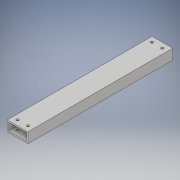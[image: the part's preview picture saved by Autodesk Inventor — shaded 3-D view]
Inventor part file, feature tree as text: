
AUTODESK INVENTOR PART (.ipt)
format: ipt  version: 2017 (Build 210142000, 142)  size: 117,248 bytes
history: native  units: in
note: dims shown in document units (in); Inventor stores cm internally (conversion verified against a paired STEP export)
features: sketch x2, extrude x1, hole x1
ambient origin geometry x8: Origin, YZ Plane, XZ Plane, XY Plane, X Axis, Y Axis, Z Axis, Center Point
bodies: Solid1 (feature_tree)
feature tree (4):
  extrude  "Extrusion1"  Depth=1.0in
  hole  "Hole1"  [1 undecoded]
  sketch  "Sketch1"  dims[d0=2.0in d1=1.0in]
  sketch  "Sketch2"  dims[d2=1.75in d3=0.75in d4=0.125in d5=0.125in d6=14.0in d7=0.0in d8=0.25in d9=0.5in d10=0.5in d11=0.25in d12=0.75in d13=0.375in d14=0.25in d15=0.5635in d16=1.0in d17=0.8108in]
note: 1 required parameter value undecoded (feature->parameter linkage not recoverable at this tier; creation-order binding heuristic only, values carry confidence <= 0.55)
